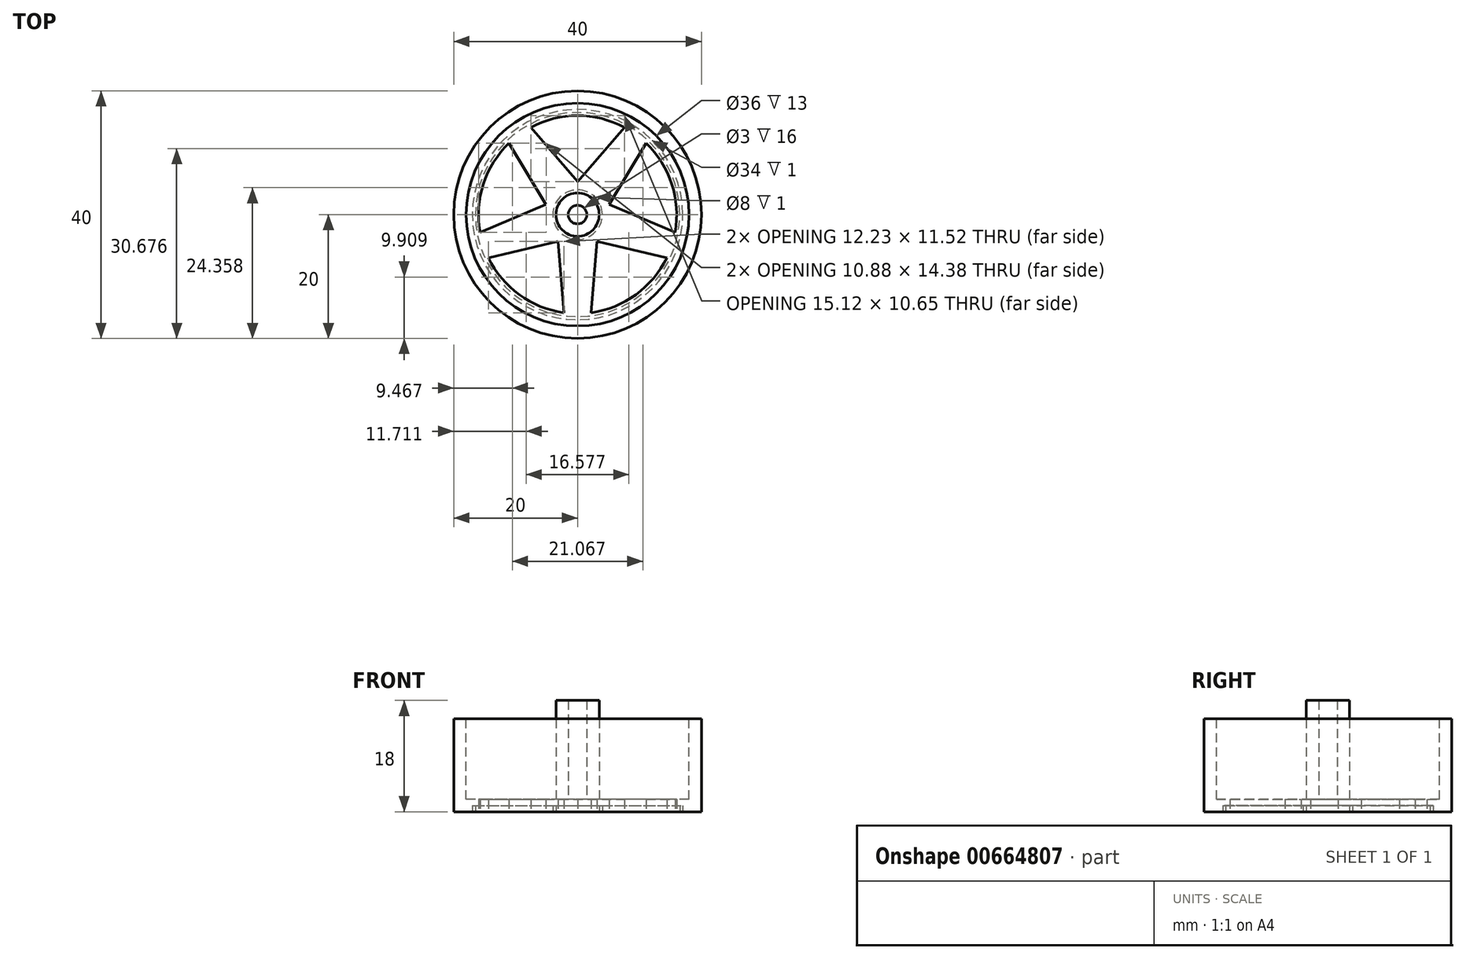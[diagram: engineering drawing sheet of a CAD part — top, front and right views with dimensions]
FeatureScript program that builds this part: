
annotation { "Feature Type Name" : "Feature", "Feature Type Description" : "" }
export const myFeature = defineFeature(function(context is Context, id is Id, definition is map)
    precondition{}
    {
        {
            var Q0;
            Q0=qCreatedBy(makeId("Top.planeOp"),FACE);
            var sketch = newSketch(context, id + "F0", { "sketchPlane" : qUnion([Q0])});
            skCircle(sketch, "E0", {"center": v(0, 0) * mm, "radius": 20 * mm});
            skSolve(sketch);
        }
        {
            var Q0;
            Q0=makeQuery(id+"F0.imprint","IMPRINT",FACE,{"disambiguationData":[TD([[makeQuery(id+"F0.imprint","IMPRINT",EDGE,{"derivedFrom":sQuery(id+"F0.wireOp",EDGE,"E0")}),1.0]])]});
            extrude(context, id + "F1", {"entities" : qUnion([Q0]), "depth" : 15 * mm, "offsetDistance" : 25 * mm});
        }
        {
            var Q0;
            Q0=makeQuery(id+"F1.opExtrude","CAP_FACE",FACE,{"disambiguationData":[OSD([sQuery(id+"F0.wireOp",EDGE,"E0")])],"isStart":false});
            var sketch = newSketch(context, id + "F2", { "sketchPlane" : qUnion([Q0])});
            skCircle(sketch, "E1", {"center": v(0, 0) * mm, "radius": 18 * mm});
            skSolve(sketch);
        }
        {
            var Q0;
            Q0=makeQuery(id+"F2.imprint","IMPRINT",FACE,{"disambiguationData":[TD([[makeQuery(id+"F2.imprint","IMPRINT",EDGE,{"derivedFrom":sQuery(id+"F2.wireOp",EDGE,"E1")}),1.0]])]});
            extrude(context, id + "F3", {"entities" : qUnion([Q0]), "operationType" : NewBodyOperationType.REMOVE, "oppositeDirection" : true, "depth" : 13 * mm, "offsetDistance" : 25 * mm});
        }
        {
            var Q0;
            Q0=makeQuery(id+"F3.boolean.opBoolean","COPY",FACE,{"derivedFrom":makeQuery(id+"F3.opExtrude","CAP_FACE",FACE,{"disambiguationData":[OSD([sQuery(id+"F2.wireOp",EDGE,"E1")])],"isStart":false})});
            var sketch = newSketch(context, id + "F4", { "sketchPlane" : qUnion([Q0])});
            skCircle(sketch, "E2", {"center": v(0, 0) * mm, "radius": 1.5 * mm});
            skCircle(sketch, "E3", {"center": v(0, 0) * mm, "radius": 3.5 * mm});
            skSolve(sketch);
        }
        {
            var Q0;
            Q0=makeQuery(id+"F1.opExtrude","CAP_FACE",FACE,{"disambiguationData":[OSD([sQuery(id+"F0.wireOp",EDGE,"E0")])],"isStart":true});
            var sketch = newSketch(context, id + "F5", { "sketchPlane" : qUnion([Q0])});
            skLineSegment(sketch, "E4", {"start": v(0, 0) * mm, "end": v(2, 0) * mm});
            skLineSegment(sketch, "E5", {"start": v(2.17, 15.85) * mm, "end": v(3.15, 4.33) * mm});
            skLineSegment(sketch, "E6.MirrorCS", {"start": v(-2.17, 15.85) * mm, "end": v(-3.15, 4.33) * mm});
            skLineSegment(sketch, "E7.1.0", {"start": v(-15.75, 2.83) * mm, "end": v(-5.1, -1.65) * mm});
            skLineSegment(sketch, "E7.1.4", {"start": v(-14.4, 6.96) * mm, "end": v(-3.15, 4.33) * mm});
            skLineSegment(sketch, "E7.2.0", {"start": v(-7.56, -14.1) * mm, "end": v(0, -5.35) * mm});
            skLineSegment(sketch, "E7.2.4", {"start": v(-11.07, -11.55) * mm, "end": v(-5.1, -1.65) * mm});
            skLineSegment(sketch, "E7.3.0", {"start": v(11.07, -11.55) * mm, "end": v(5.1, -1.65) * mm});
            skLineSegment(sketch, "E7.3.4", {"start": v(7.56, -14.1) * mm, "end": v(0, -5.35) * mm});
            skLineSegment(sketch, "E7.4.0", {"start": v(14.4, 6.96) * mm, "end": v(3.15, 4.33) * mm});
            skLineSegment(sketch, "E7.4.4", {"start": v(15.75, 2.83) * mm, "end": v(5.1, -1.65) * mm});
            skPoint(sketch, "E7.center", {"position": v(0, 0) * mm});
            skArc(sketch, "E8", {"start": v(-2.17, 15.85) * mm, "mid": v(-9.4, 12.94) * mm, "end": v(-14.4, 6.96) * mm});
            skPoint(sketch, "E9.orphan", {"position": v(-2, 17.89) * mm});
            skPoint(sketch, "E10.trimOffspring.end.orphan", {"position": v(2, 17.89) * mm});
            skPoint(sketch, "E11.orphan", {"position": v(16.4, 7.43) * mm});
            skPoint(sketch, "E12.orphan", {"position": v(17.63, 3.63) * mm});
            skPoint(sketch, "E13.orphan", {"position": v(12.13, -13.3) * mm});
            skPoint(sketch, "E14.orphan", {"position": v(-8.9, -15.65) * mm});
            skPoint(sketch, "E15.orphan", {"position": v(-17.63, 3.63) * mm});
            skPoint(sketch, "E16.orphan", {"position": v(-16.4, 7.43) * mm});
            skCircle(sketch, "E17", {"center": v(0, 0) * mm, "radius": 16.5 * mm});
            skCircle(sketch, "E18", {"center": v(0, 0) * mm, "radius": 17 * mm});
            skArc(sketch, "E19.trimOffspring", {"start": v(14.4, 6.96) * mm, "mid": v(9.4, 12.94) * mm, "end": v(2.17, 15.85) * mm});
            skArc(sketch, "E20.trimOffspring", {"start": v(11.07, -11.55) * mm, "mid": v(15.22, -4.94) * mm, "end": v(15.75, 2.83) * mm});
            skArc(sketch, "E21.trimOffspring", {"start": v(-7.56, -14.1) * mm, "mid": v(0, -16) * mm, "end": v(7.56, -14.1) * mm});
            skArc(sketch, "E22.trimOffspring", {"start": v(-15.75, 2.83) * mm, "mid": v(-15.22, -4.94) * mm, "end": v(-11.07, -11.55) * mm});
            skSolve(sketch);
        }
        {
            var Q0;
            Q0=makeQuery(id+"F4.imprint","IMPRINT",FACE,{"disambiguationData":[TD([[makeQuery(id+"F4.imprint","IMPRINT",EDGE,{"derivedFrom":sQuery(id+"F4.wireOp",EDGE,"E2")}),-1.0]])]});
            extrude(context, id + "F6", {"entities" : qUnion([Q0]), "operationType" : NewBodyOperationType.ADD, "depth" : 16 * mm, "offsetDistance" : 25 * mm});
        }
        {
            var Q0;
            Q0=makeQuery(id+"F5.imprint","IMPRINT",FACE,{"disambiguationData":[TD([[makeQuery(id+"F5.imprint","IMPRINT",EDGE,{"derivedFrom":sQuery(id+"F5.wireOp",EDGE,"E7.2.0")}),-1.0]])]});
            var Q1;
            Q1=makeQuery(id+"F5.imprint","IMPRINT",FACE,{"disambiguationData":[TD([[makeQuery(id+"F5.imprint","IMPRINT",EDGE,{"derivedFrom":sQuery(id+"F5.wireOp",EDGE,"E7.1.0")}),-1.0]])]});
            var Q2;
            Q2=makeQuery(id+"F5.imprint","IMPRINT",FACE,{"disambiguationData":[TD([[makeQuery(id+"F5.imprint","IMPRINT",EDGE,{"derivedFrom":sQuery(id+"F5.wireOp",EDGE,"E6.MirrorCS")}),-1.0]])]});
            var Q3;
            Q3=makeQuery(id+"F5.imprint","IMPRINT",FACE,{"disambiguationData":[TD([[makeQuery(id+"F5.imprint","IMPRINT",EDGE,{"derivedFrom":sQuery(id+"F5.wireOp",EDGE,"E5")}),1.0]])]});
            var Q4;
            Q4=makeQuery(id+"F5.imprint","IMPRINT",FACE,{"disambiguationData":[TD([[makeQuery(id+"F5.imprint","IMPRINT",EDGE,{"derivedFrom":sQuery(id+"F5.wireOp",EDGE,"E7.3.0")}),-1.0]])]});
            extrude(context, id + "F7", {"entities" : qUnion([Q0, Q1, Q2, Q3, Q4]), "operationType" : NewBodyOperationType.REMOVE, "oppositeDirection" : true, "depth" : 2 * mm});
        }
        {
            var Q0;
            Q0=qSketchRegion(id+"F5",true);
            extrude(context, id + "F8", {"entities" : qUnion([Q0]), "operationType" : NewBodyOperationType.REMOVE, "oppositeDirection" : true, "depth" : 1 * mm});
        }
        {
            var Q0;
            Q0=makeQuery(id+"F8.boolean.opBoolean","SPLIT",FACE,{"disambiguationData":[TD([makeQuery(id+"F7.boolean.opBoolean","COPY",FACE,{"derivedFrom":makeQuery(id+"F7.opExtrude","SWEPT_FACE",FACE,{"disambiguationData":[OSD([sQuery(id+"F5.wireOp",EDGE,"E5")])]})})])],"derivedFrom":makeQuery(id+"F1.opExtrude","CAP_FACE",FACE,{"disambiguationData":[OSD([sQuery(id+"F0.wireOp",EDGE,"E0")])],"isStart":true})});
            var sketch = newSketch(context, id + "F9", { "sketchPlane" : qUnion([Q0])});
            skCircle(sketch, "E23", {"center": v(0, 0) * mm, "radius": 3.5 * mm});
            skCircle(sketch, "E24", {"center": v(0, 0) * mm, "radius": 4 * mm});
            skSolve(sketch);
        }
        {
            var Q0;
            Q0=makeQuery(id+"F9.imprint","IMPRINT",FACE,{"disambiguationData":[TD([[makeQuery(id+"F9.imprint","IMPRINT",EDGE,{"derivedFrom":sQuery(id+"F9.wireOp",EDGE,"E23")}),-1.0]])]});
            extrude(context, id + "F10", {"entities" : qUnion([Q0]), "operationType" : NewBodyOperationType.REMOVE, "oppositeDirection" : true, "depth" : 1 * mm});
        }
    });
